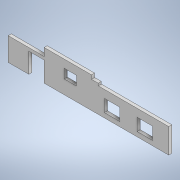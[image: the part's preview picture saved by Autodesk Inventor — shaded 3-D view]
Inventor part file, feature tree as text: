
AUTODESK INVENTOR PART (.ipt)
format: ipt  version: 2020.1 (Build 241239000, 239)  size: 153,088 bytes
history: native  units: in
note: dims shown in document units (in); Inventor stores cm internally (conversion verified against a paired STEP export)
features: extrude x1, sketch x1
ambient origin geometry x8: Origin, YZ Plane, XZ Plane, XY Plane, X Axis, Y Axis, Z Axis, Center Point
bodies: Body1 (feature_tree)
feature tree (2):
  extrude  "Extrusion2"  Depth=60.0in
  sketch  "Sketch2"  dims[d25=90.0in d26=60.0in d28=184.0in d34=274.0in d35=96.0in d36=60.0in d38=48.0in d39=60.0in d40=48.0in d41=48.0in d42=36.0in d43=26.0in d44=105.0in d45=120.0in d46=12.0in d47=12.0in d48=0.0in d51=140.0in d52=80.0in d53=484.0in]
